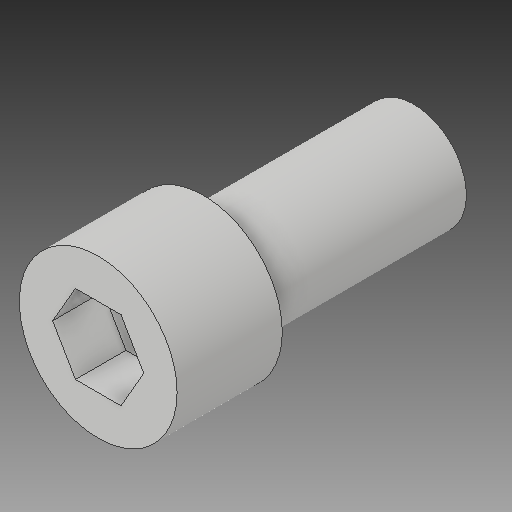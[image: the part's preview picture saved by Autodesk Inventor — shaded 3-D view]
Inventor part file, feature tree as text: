
AUTODESK INVENTOR PART (.ipt)
format: ipt  version: 2019 (Build 230136000, 136)  size: 131,072 bytes
history: native  units: in
note: dims shown in document units (in); Inventor stores cm internally (conversion verified against a paired STEP export)
features: other x13, extrude x3, sketch x3
ambient origin geometry x8: Origin, YZ Plane, XZ Plane, XY Plane, X Axis, Y Axis, Z Axis, Center Point
bodies: Solid1 (feature_tree)
feature tree (19):
  other  "Table"
  other  "shcs-025-0500"
  other  "shcs-025-0750"
  other  "shcs-025-1000"
  other  "shcs-025-1250"
  other  "shcs-025-1500"
  other  "shcs-025-1750"
  other  "shcs-025-2000"
  other  "shcs-025-2250"
  other  "shcs-025-2500"
  other  "shcs-025-3000"
  other  "shcs-025-3500"
  other  "shcs-025-4000"
  extrude  "Extrusion1"  TaperAngle=0.0deg  [1 undecoded]
  extrude  "Extrusion2"  [1 undecoded]
  extrude  "Extrusion3"  [1 undecoded]
  sketch  "Sketch1"  dims[d1=0.0in d4=0.0in]
  sketch  "Sketch2"  dims[d7=0.0in]
  sketch  "Sketch3"
note: 3 required parameter values undecoded (feature->parameter linkage not recoverable at this tier; creation-order binding heuristic only, values carry confidence <= 0.55)
